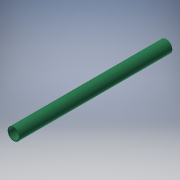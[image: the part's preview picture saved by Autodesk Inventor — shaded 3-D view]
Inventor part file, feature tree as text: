
AUTODESK INVENTOR PART (.ipt)
format: ipt  version: 2016 (Build 200138000, 138)  size: 110,592 bytes
history: native  units: in
note: dims shown in document units (in); Inventor stores cm internally (conversion verified against a paired STEP export)
features: extrude x1, sketch x1
ambient origin geometry x8: Origin, YZ Plane, XZ Plane, XY Plane, X Axis, Y Axis, Z Axis, Center Point
bodies: Solid1 (feature_tree)
feature tree (2):
  extrude  "Extrusion1"  Depth=19.685in TaperAngle=0.0deg
  sketch  "Sketch1"  dims[d1=0.1181in d2=19.685in d3=0.0in d4=1.5748in]
